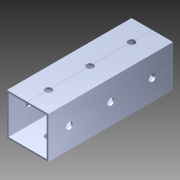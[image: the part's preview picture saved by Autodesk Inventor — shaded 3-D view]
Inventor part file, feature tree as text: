
AUTODESK INVENTOR PART (.ipt)
format: ipt  version: 2014 (Build 180170000, 170)  size: 1,124,352 bytes
history: native  units: in
note: dims shown in document units (in); Inventor stores cm internally (conversion verified against a paired STEP export)
features: pattern_circular x1, other x1, plane x1, extrude x1, imported_body x1, sketch x1
ambient origin geometry x8: Origin, YZ Plane, XZ Plane, XY Plane, X Axis, Y Axis, Z Axis, Center Point
bodies: Body1 (feature_tree)
feature tree (6):
  pattern_circular  "CirPattern2"
  other  "217-3426-STEP1"
  plane  "Work Plane1"
  extrude  "Extrusion1"  Depth=3937.0079in TaperAngle=0.0deg
  imported_body  "Base1"
  sketch  "Sketch1"  dims[d0=-3.0in d1=3937.0079in d2=0.0in]
